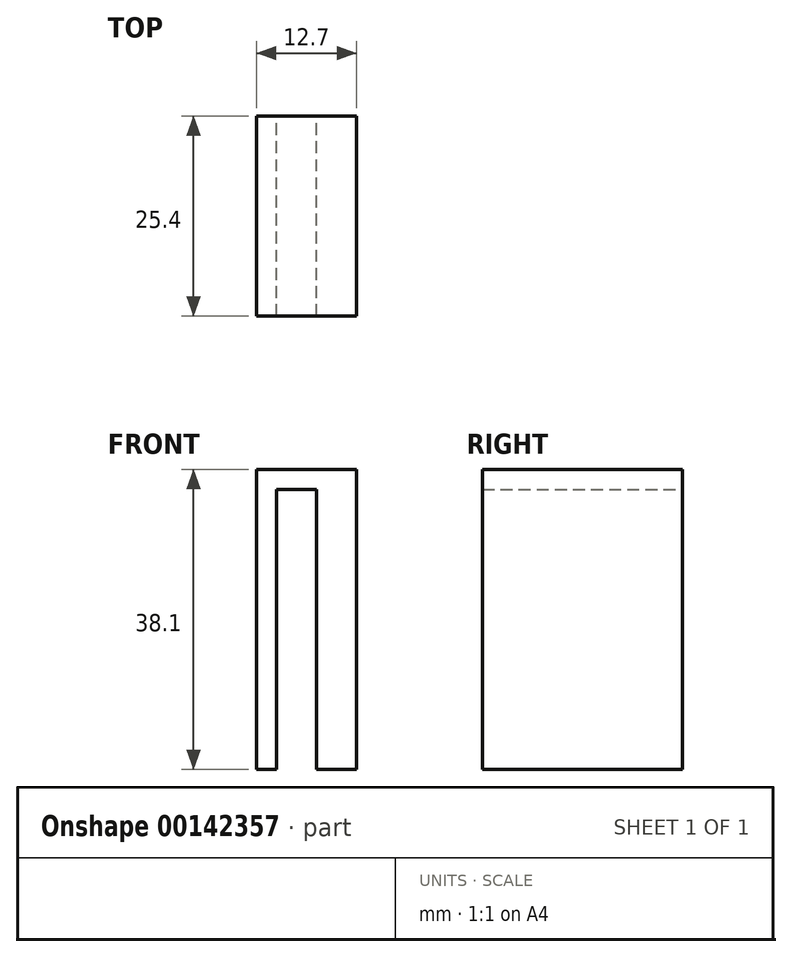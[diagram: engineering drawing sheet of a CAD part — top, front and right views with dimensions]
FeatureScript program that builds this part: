
annotation { "Feature Type Name" : "Feature", "Feature Type Description" : "" }
export const myFeature = defineFeature(function(context is Context, id is Id, definition is map)
    precondition{}
    {
        {
            var Q0;
            Q0=qCreatedBy(makeId("Front.planeOp"),FACE);
            var sketch = newSketch(context, id + "F0", { "sketchPlane" : qUnion([Q0])});
            skLineSegment(sketch, "E0.bottom", {"start": v(-9.53, 0) * mm, "end": v(3.17, 0) * mm});
            skLineSegment(sketch, "E0.top", {"start": v(-9.53, 38.1) * mm, "end": v(3.17, 38.1) * mm});
            skLineSegment(sketch, "E0.left", {"start": v(-9.53, 0) * mm, "end": v(-9.53, 38.1) * mm});
            skLineSegment(sketch, "E0.right", {"start": v(3.17, 0) * mm, "end": v(3.17, 38.1) * mm});
            skLineSegment(sketch, "E1.bottom", {"start": v(-6.99, 0) * mm, "end": v(-1.9, 0) * mm});
            skLineSegment(sketch, "E1.top", {"start": v(-6.99, 35.56) * mm, "end": v(-1.9, 35.56) * mm});
            skLineSegment(sketch, "E1.left", {"start": v(-6.99, 0) * mm, "end": v(-6.99, 35.56) * mm});
            skLineSegment(sketch, "E1.right", {"start": v(-1.9, 0) * mm, "end": v(-1.9, 35.56) * mm});
            skSolve(sketch);
        }
        {
            var Q0;
            Q0=makeQuery(id+"F0.imprint","IMPRINT",FACE,{"disambiguationData":[TD([[makeQuery(id+"F0.imprint","IMPRINT",EDGE,{"derivedFrom":sQuery(id+"F0.wireOp",EDGE,"E0.top")}),-1.0]])]});
            extrude(context, id + "F1", {"entities" : qUnion([Q0]), "depth" : 25.4 * mm});
        }
    });
